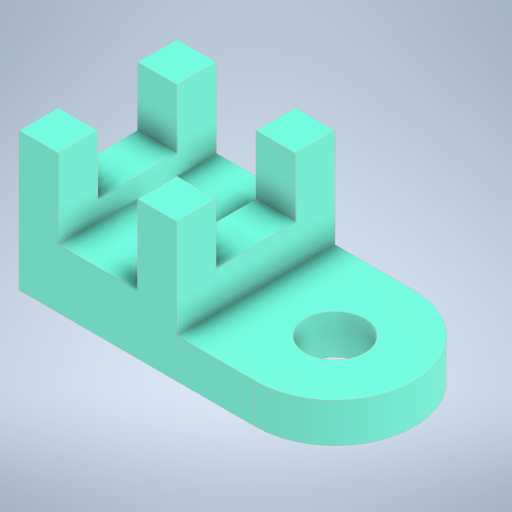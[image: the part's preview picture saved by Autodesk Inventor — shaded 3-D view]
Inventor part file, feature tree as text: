
AUTODESK INVENTOR PART (.ipt)
format: ipt  version: 2024 (Build 280153000, 153)  size: 287,232 bytes
history: native  units: in
note: dims shown in document units (in); Inventor stores cm internally (conversion verified against a paired STEP export)
features: extrude x4, other x4
ambient origin geometry x8: Origin, YZ Plane, XZ Plane, XY Plane, X Axis, Y Axis, Z Axis, Center Point
bodies: Solid1 (feature_tree)
feature tree (8):
  extrude  "SIDE PROFILE EXTRUSION"  Depth=3.0in
  extrude  "FRONT ROUNDING"  Depth=1.5in
  extrude  "HOLE CUTOUT"  Depth=1.75in
  extrude  "RECTANGULAR CUTOUT"  Depth=0.5in
  other  "SIDE PROFILE"
  other  "SEMICIRCLE"
  other  "CIRCLE"
  other  "RECTANGLE"
